# Revit family: HBF_Eng
name_source: partatom
category: Оборудование
units: mm (PartAtom-declared; Revit-internal decimal feet)

## family parameters
Всегда вертикально = Да
Классификация = Нет
На основе рабочей плоскости = Нет
Общий = Нет
При загрузке вырезать с полостями = Нет
Размер круглого соединителя = Использовать диаметр
Тип детали = Нормальный
Точка принадлежности помещению = Нет

## types (4) — shared parameters
00_20_Manufacturer = Vents
00_20_Name = Ceiling exhaust fan
Amperage = 0 А
Casing Material = Plastic, opaque, black
D = 316 мм
Diameter = 316 мм
Dn = 150 мм
Dy = 145 мм
Frequency = 50 Гц
H = 198 мм
H1 = 22 мм
Height = 236 мм
Length = 330 мм
Load Classification = HVAC
Maintenance zone material = <По категории>
Maximum Air Flow = 482.0 м³/ч
Number of Fase = 1
Power = 57 Вт
R = 158 мм
R1 = 125 мм
R2 = 115 мм
R3 = 165 мм
Sound pressure level at 3 m distance = 36 dBA
URL = https://ventilation-system.com
Voltage = 220 В
Width = 330 мм
h = 101 мм
h1 = 166 мм
r = 53 мм
r1 = 70 мм
r2 = 151 мм
Изготовитель = Vents
zero-valued in all types: Отметка по умолчанию

## per-type parameters (varying)
| type | Circle Lid | Grid Material | Rectangle Lid |
| HBF 250 Square | Нет | Plastic, opaque, white | Да |
| HBF 250 Round | Да | Plastic, opaque, white | Нет |
| HBF 250 Round Black | Да | Plastic, opaque, black | Нет |
| HBF 250 Square Black | Нет | Plastic, opaque, black | Да |

note: column(s) folded — value = type name in every type: 00_20_Type
